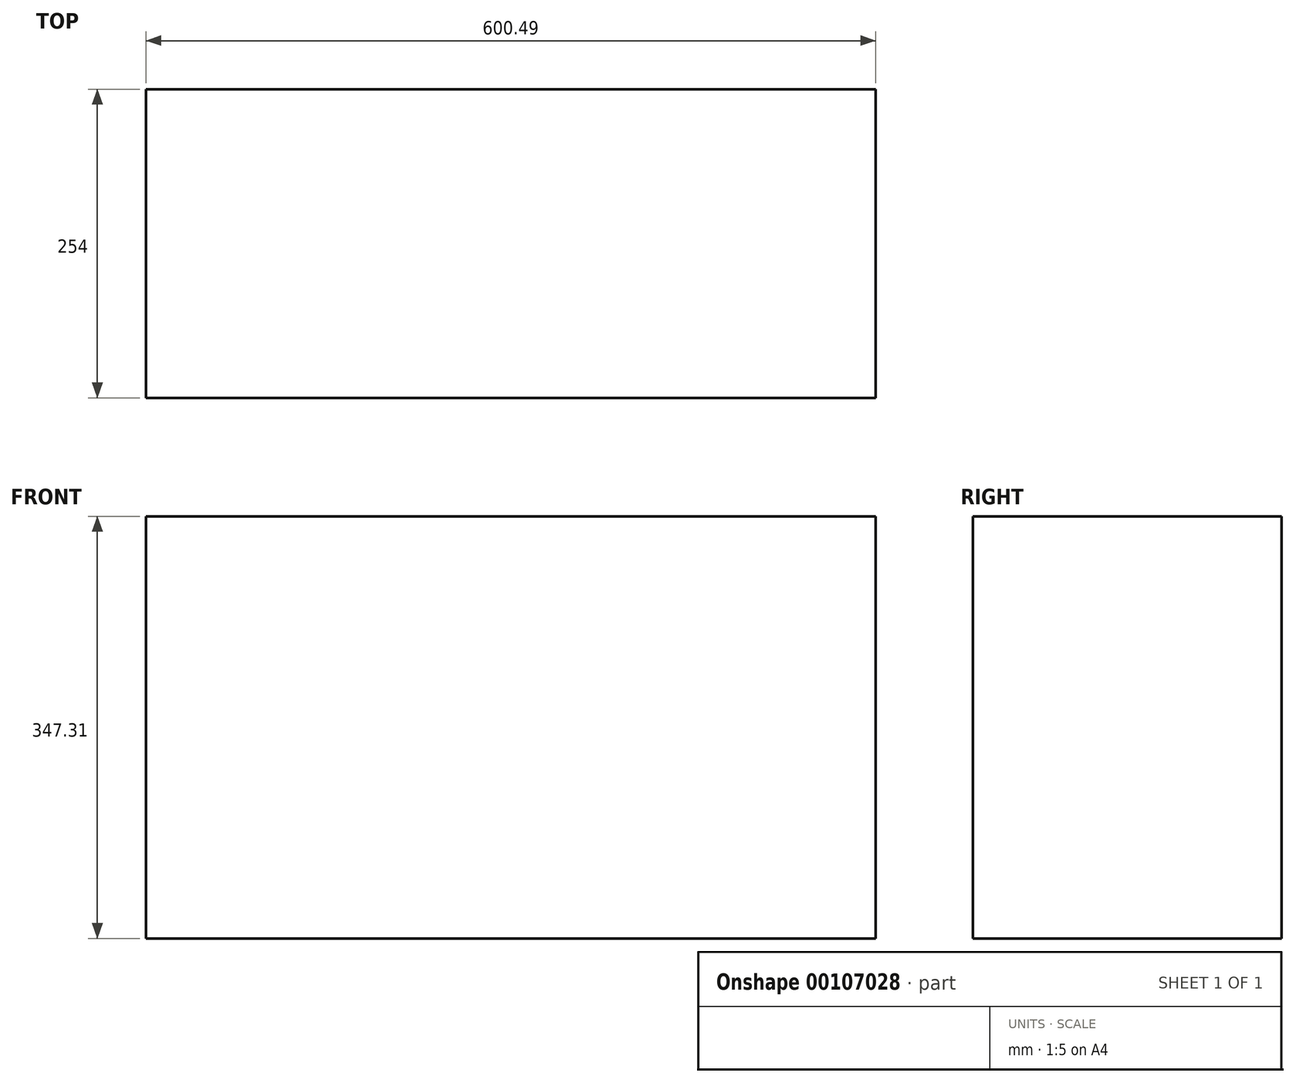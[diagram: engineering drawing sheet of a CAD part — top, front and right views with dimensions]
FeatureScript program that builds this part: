
annotation { "Feature Type Name" : "Feature", "Feature Type Description" : "" }
export const myFeature = defineFeature(function(context is Context, id is Id, definition is map)
    precondition{}
    {
        {
            var Q0;
            Q0=qCreatedBy(makeId("Front.planeOp"),FACE);
            var sketch = newSketch(context, id + "F0", { "sketchPlane" : qUnion([Q0])});
            skLineSegment(sketch, "E0.bottom", {"start": v(0, 0) * mm, "end": v(-600.5, 0) * mm});
            skLineSegment(sketch, "E0.top", {"start": v(0, -347.31) * mm, "end": v(-600.5, -347.31) * mm});
            skLineSegment(sketch, "E0.left", {"start": v(0, 0) * mm, "end": v(0, -347.31) * mm});
            skLineSegment(sketch, "E0.right", {"start": v(-600.5, 0) * mm, "end": v(-600.5, -347.31) * mm});
            skSolve(sketch);
        }
        {
            var Q0;
            Q0=makeQuery(id+"F0.imprint","IMPRINT",FACE,{"disambiguationData":[TD([[makeQuery(id+"F0.imprint","IMPRINT",EDGE,{"derivedFrom":sQuery(id+"F0.wireOp",EDGE,"E0.bottom")}),1.0]])]});
            extrude(context, id + "F1", {"entities" : qUnion([Q0]), "depth" : 254 * mm});
        }
    });
